# Revit family: Varmax Twin 640_4 tomas
name_source: partatom
category: Mechanical Equipment
revit_build: Autodesk Revit 2014 (Build: 20130308_1515(x64)
units: mm (PartAtom-declared; Revit-internal decimal feet)

## types (1)
- Varmax Twin 640 - Caldera de pie de condensación a gas 676 kW y 6 bar (4 tomas)
    Altura = 1877 mm  [stored 6.15814 ft]
    Ancho = 2259 mm  [stored 7.41142 ft]
    Ancho total = 2519 mm  [stored 8.26444 ft]
    Assembly Code = D3020100
    Configuración = 4 tomas
    Consumo eléctrico máximo = 704 W
    Description = Unidad térmica de condensación para gas natural Ygnis modelo Varmax 640,  potencia útil (50/30 ºC) de 676 kW. Fabricada en acero inoxidable de alta calidad AISI 316 L. Quemador modulante desde el 10% de la potencia. Rendimiento hasta el 108 %. Clase 5 de NOx. Dimensiones (Altura x Ancho x Largo): 1877 x 2259 x 2032 mm. Peso en vacío: 1050 kg. Presión máxima de servicio: 6 bar. Configuración a 4 tomas.
centralizadas en edificios de viviendas, complejos de
oficinas o centros deportivos.  solución
flexible, eficiente y versátil. Se compone de dos calderas
Varmax con potencias comprendidas entre los 536 y
956 kW para dar cobertura a aquellas instalaciones que
precisan grandes demandas de ACS y calefacción. Se
compone de dos calderas iguales en potencia, un kit de
evacuación de humos a una sola chimenea y regulación
Navistem para la gestión en cascada.
    Diametro = 250 mm  [stored 0.82021 ft]
    Dist. = 450 mm
    Empresa creadora del BIM = ACAE
    Manufacturer = Atlantic
    Model = Varmax Twin 640
    Mínimo = 45 mm
    Peso en vacío = 1050 kg
    Potencia útil (50/30 ºC) = 676 kW
    Potencia útil a 80/60 ºC = 624 kW
    Presión máxima de servicio = 6 bar
    Profundidad = 2032 mm
    Rendimiento mínimo al 100% de = 97,9%
    Rendimiento mínimo al 30% de carga = 108%
    Tipo de combustible = Gas natural (G20)
    URL = http://www.ygnis.es
    Volumen de agua = 478 L

note: [stored X ft] marks values corroborated as IEEE doubles in the binary element streams (Revit-internal decimal feet)

## geometry (parser evidence)
native form markers: Sweep x2
no freeform markers — native parametric forms only
